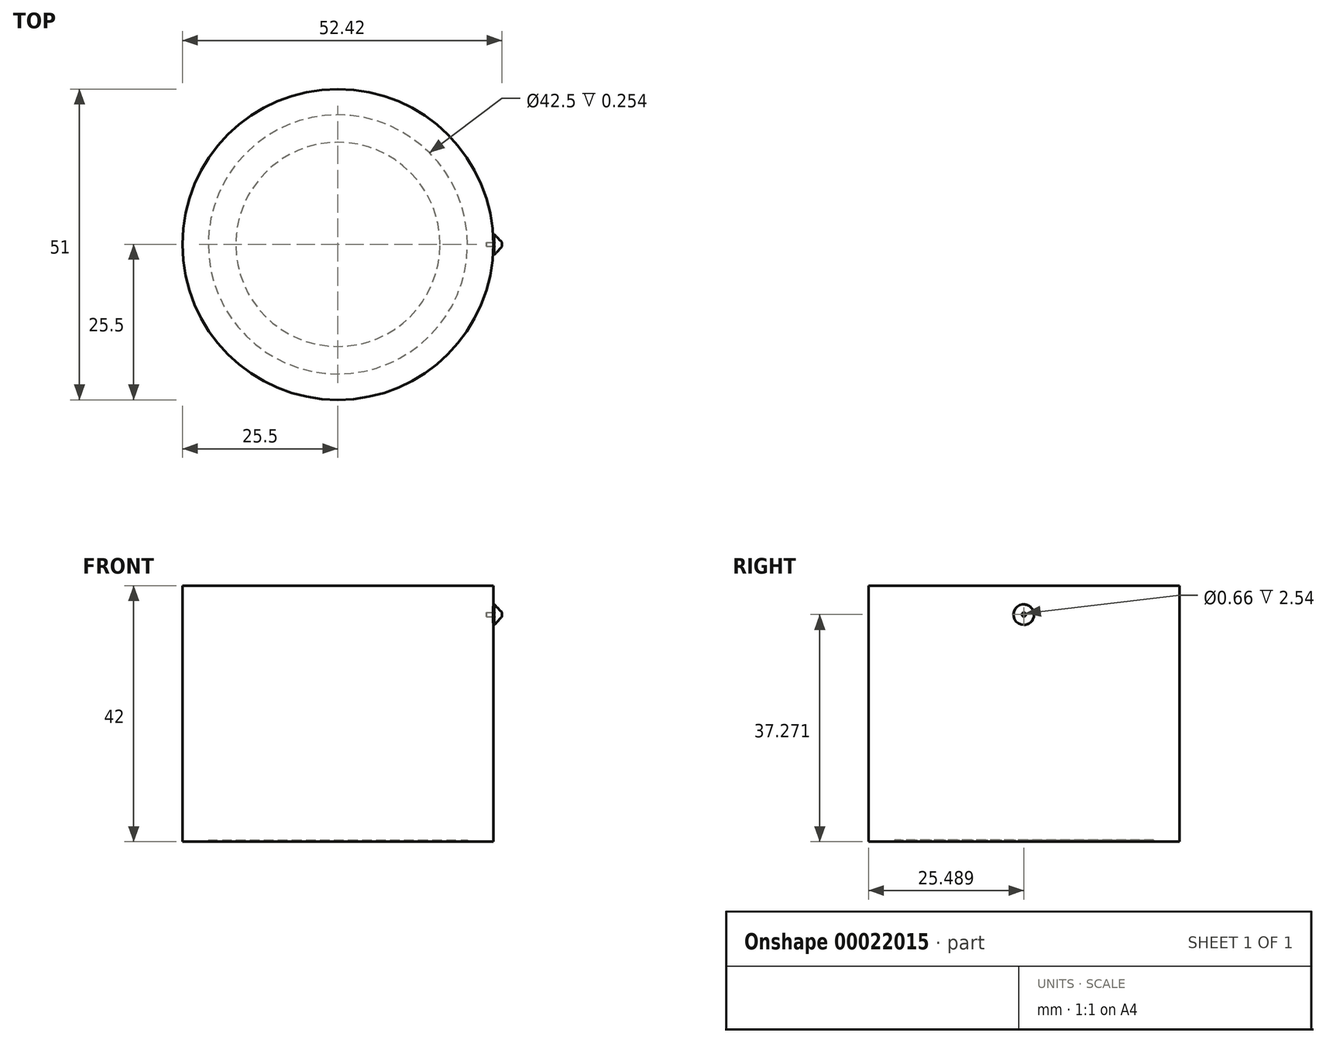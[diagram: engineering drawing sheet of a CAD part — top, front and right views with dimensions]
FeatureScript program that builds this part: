
annotation { "Feature Type Name" : "Feature", "Feature Type Description" : "" }
export const myFeature = defineFeature(function(context is Context, id is Id, definition is map)
    precondition{}
    {
        {
            var Q0;
            Q0=qCreatedBy(makeId("Top.planeOp"),FACE);
            var sketch = newSketch(context, id + "F0", { "sketchPlane" : qUnion([Q0])});
            skCircle(sketch, "E0", {"center": v(0, 0) * mm, "radius": 25.5 * mm});
            skSolve(sketch);
        }
        {
            var Q0;
            Q0 = qSketchRegion(id + "F0", true);
            extrude(context, id + "F1", {"entities" : qUnion([Q0]), "depth" : 42 * mm});
        }
        {
            var Q0;
            Q0=makeQuery(id+"F1.opExtrude","CAP_FACE",FACE,{"disambiguationData":[OSD([sQuery(id+"F0.wireOp",EDGE,"E0")])],"isStart":true});
            var sketch = newSketch(context, id + "F2", { "sketchPlane" : qUnion([Q0])});
            skCircle(sketch, "E1", {"center": v(0, 0) * mm, "radius": 21.25 * mm});
            skCircle(sketch, "E2", {"center": v(0, 0) * mm, "radius": 16.75 * mm});
            skSolve(sketch);
        }
        {
            var Q0;
            Q0 = qSketchRegion(id + "F2", true);
            extrude(context, id + "F3", {"entities" : qUnion([Q0]), "operationType" : NewBodyOperationType.REMOVE, "oppositeDirection" : true, "depth" : 0.25 * mm});
        }
        {
            var Q0;
            Q0=qCreatedBy(makeId("Right.planeOp"),FACE);
            cPlane(context, id + "F4", {"entities" : qUnion([Q0]), "cplaneType" : CPlaneType.OFFSET, "offset" : 25.65 * mm, "width" : 152.4 * mm, "height" : 152.4 * mm});
        }
        {
            var Q0;
            Q0=qCreatedBy(id+"F4.planeOp",FACE);
            var sketch = newSketch(context, id + "F5", { "sketchPlane" : qUnion([Q0])});
            skCircle(sketch, "E3", {"center": v(-0.03, 37.25) * mm, "radius": 1.69 * mm});
            skSolve(sketch);
        }
        {
            var Q0;
            Q0 = qSketchRegion(id + "F5", true);
            extrude(context, id + "F6", {"entities" : qUnion([Q0]), "operationType" : NewBodyOperationType.ADD, "oppositeDirection" : true, "depth" : 25.4 * mm});
        }
        {
            var Q0;
            Q0=makeQuery(id+"F6.opExtrude","CAP_FACE",FACE,{"disambiguationData":[OSD([sQuery(id+"F5.wireOp",EDGE,"E3")])],"isStart":true});
            cPlane(context, id + "F7", {"entities" : qUnion([Q0]), "cplaneType" : CPlaneType.OFFSET, "offset" : 1.27 * mm, "width" : 152.4 * mm, "height" : 152.4 * mm});
        }
        {
            var Q0;
            Q0=qCreatedBy(id+"F7.planeOp",FACE);
            var sketch = newSketch(context, id + "F8", { "sketchPlane" : qUnion([Q0])});
            skCircle(sketch, "E4", {"center": v(-0.01, 37.27) * mm, "radius": 0.33 * mm});
            skSolve(sketch);
        }
        {
            var Q1;
            Q1=makeQuery(id+"F6.opExtrude","CAP_FACE",FACE,{"disambiguationData":[OSD([sQuery(id+"F5.wireOp",EDGE,"E3")])],"isStart":true});
            var Q2;
            Q2=makeQuery(id+"F8.imprint","IMPRINT",FACE,{"disambiguationData":[TD([[makeQuery(id+"F8.imprint","IMPRINT",EDGE,{"derivedFrom":sQuery(id+"F8.wireOp",EDGE,"E4")}),1.0]])]});
            loft(context, id + "F9", {"operationType" : NewBodyOperationType.ADD, "sheetProfilesArray" : [{ "sheetProfileEntities" : qUnion([Q1]) }, { "sheetProfileEntities" : qUnion([Q2]) }]});
        }
        {
            var Q0;
            Q0=makeQuery(id+"F9.opLoft","CAP_FACE",FACE,{"disambiguationData":[OSD([makeQuery(id+"F8.imprint","IMPRINT",FACE,{"disambiguationData":[TD([[makeQuery(id+"F8.imprint","IMPRINT",EDGE,{"derivedFrom":sQuery(id+"F8.wireOp",EDGE,"E4")}),1.0]])]})])],"isStart":true});
            extrude(context, id + "F10", {"entities" : qUnion([Q0]), "operationType" : NewBodyOperationType.REMOVE, "oppositeDirection" : true, "depth" : 2.54 * mm});
        }
    });
